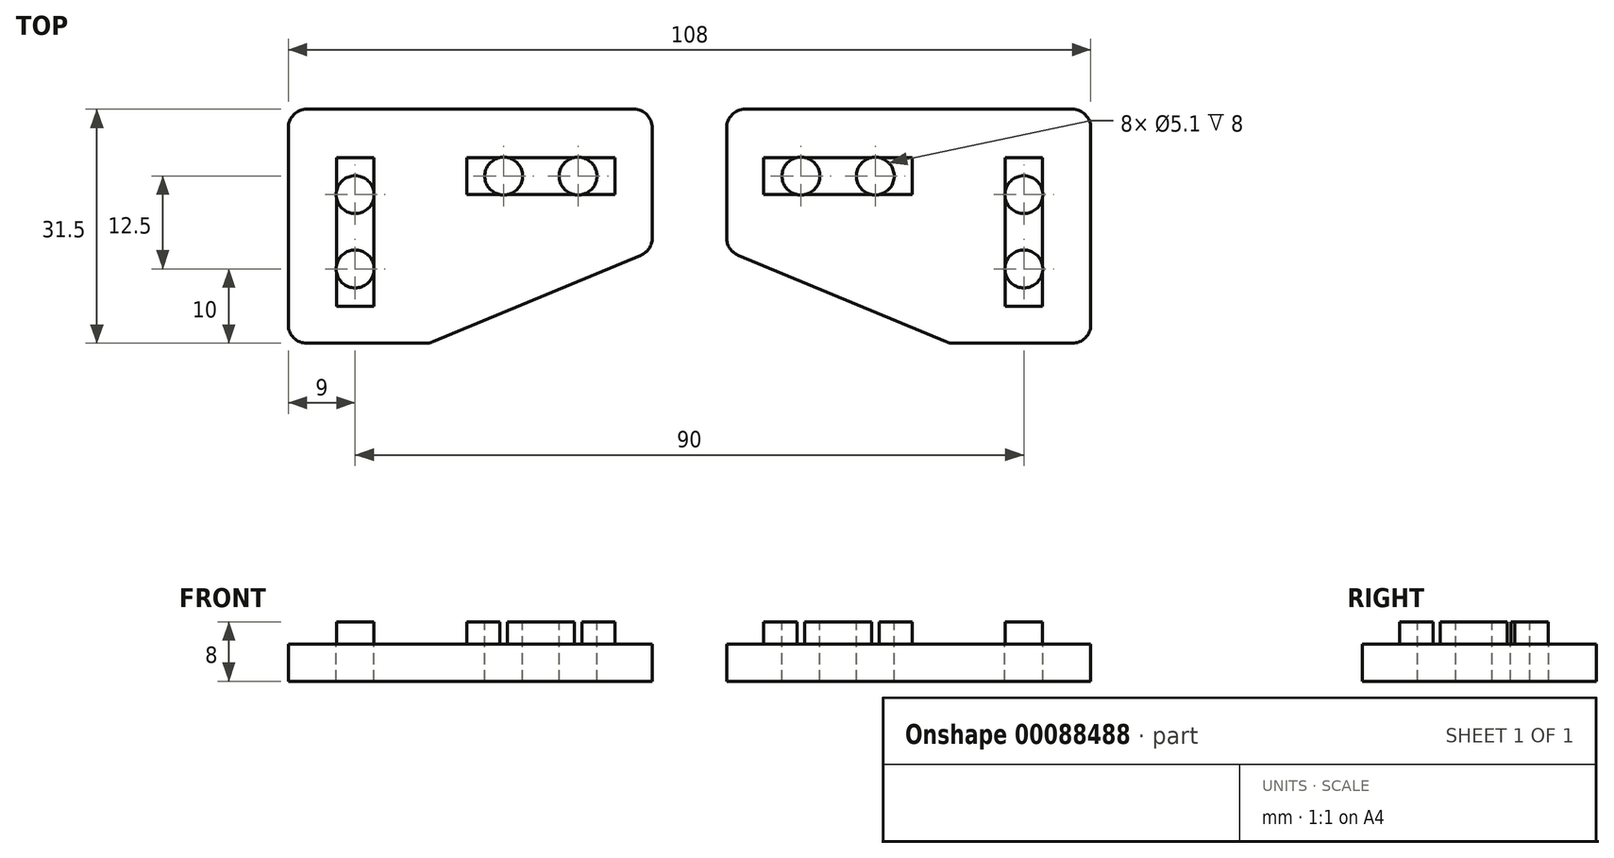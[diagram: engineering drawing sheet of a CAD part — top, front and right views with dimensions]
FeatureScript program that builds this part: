
annotation { "Feature Type Name" : "Feature", "Feature Type Description" : "" }
export const myFeature = defineFeature(function(context is Context, id is Id, definition is map)
    precondition{}
    {
        {
            var Q0;
            Q0=qCreatedBy(makeId("Top.planeOp"),FACE);
            var sketch = newSketch(context, id + "F0", { "sketchPlane" : qUnion([Q0])});
            skLineSegment(sketch, "E0", {"start": v(-9, -1) * mm, "end": v(40, -1) * mm});
            skLineSegment(sketch, "E1", {"start": v(40, -1) * mm, "end": v(40, -20) * mm});
            skLineSegment(sketch, "E2", {"start": v(-9, -1) * mm, "end": v(-9, -32.5) * mm});
            skLineSegment(sketch, "E3", {"start": v(-9, -32.5) * mm, "end": v(10, -32.5) * mm});
            skLineSegment(sketch, "E4.bottom", {"start": v(2.5, -7.5) * mm, "end": v(-2.5, -7.5) * mm, "construction": true});
            skLineSegment(sketch, "E4.top", {"start": v(2.5, -27.5) * mm, "end": v(-2.5, -27.5) * mm, "construction": true});
            skLineSegment(sketch, "E4.left", {"start": v(2.5, -7.5) * mm, "end": v(2.5, -27.5) * mm, "construction": true});
            skLineSegment(sketch, "E4.right", {"start": v(-2.5, -7.5) * mm, "end": v(-2.5, -27.5) * mm, "construction": true});
            skPoint(sketch, "E4.middle", {"position": v(0, -17.5) * mm});
            skLineSegment(sketch, "E5.bottom", {"start": v(15, -7.5) * mm, "end": v(35, -7.5) * mm, "construction": true});
            skLineSegment(sketch, "E5.top", {"start": v(15, -12.5) * mm, "end": v(35, -12.5) * mm, "construction": true});
            skLineSegment(sketch, "E5.left", {"start": v(15, -7.5) * mm, "end": v(15, -12.5) * mm, "construction": true});
            skLineSegment(sketch, "E5.right", {"start": v(35, -7.5) * mm, "end": v(35, -12.5) * mm, "construction": true});
            skPoint(sketch, "E5.middle", {"position": v(25, -10) * mm});
            skLineSegment(sketch, "E6", {"start": v(10, -32.5) * mm, "end": v(40, -20) * mm});
            skSolve(sketch);
        }
        {
            var Q0;
            Q0=makeQuery(id+"F0.imprint","IMPRINT",FACE,{"disambiguationData":[TD([[makeQuery(id+"F0.imprint","IMPRINT",EDGE,{"derivedFrom":sQuery(id+"F0.wireOp",EDGE,"E0")}),-1.0]])]});
            extrude(context, id + "F1", {"entities" : qUnion([Q0]), "oppositeDirection" : true, "depth" : 5 * mm});
        }
        {
            var Q0;
            Q0=qCreatedBy(makeId("Top.planeOp"),FACE);
            var sketch = newSketch(context, id + "F2", { "sketchPlane" : qUnion([Q0])});
            skLineSegment(sketch, "E7.0", {"start": v(2.5, -7.5) * mm, "end": v(-2.5, -7.5) * mm});
            skLineSegment(sketch, "E8.0", {"start": v(-2.5, -7.5) * mm, "end": v(-2.5, -27.5) * mm});
            skLineSegment(sketch, "E9.0", {"start": v(2.5, -7.5) * mm, "end": v(2.5, -27.5) * mm});
            skLineSegment(sketch, "E10.0", {"start": v(2.5, -27.5) * mm, "end": v(-2.5, -27.5) * mm});
            skLineSegment(sketch, "E11.0", {"start": v(15, -7.5) * mm, "end": v(15, -12.5) * mm});
            skLineSegment(sketch, "E12.0", {"start": v(15, -7.5) * mm, "end": v(35, -7.5) * mm});
            skLineSegment(sketch, "E13.0", {"start": v(15, -12.5) * mm, "end": v(35, -12.5) * mm});
            skLineSegment(sketch, "E14.0", {"start": v(35, -7.5) * mm, "end": v(35, -12.5) * mm});
            skSolve(sketch);
        }
        {
            var Q0;
            Q0 = qSketchRegion(id + "F2", true);
            extrude(context, id + "F3", {"entities" : qUnion([Q0]), "operationType" : NewBodyOperationType.ADD, "depth" : 3 * mm});
        }
        {
            var Q0;
            Q0=makeQuery(id+"F3.opExtrude","CAP_FACE",FACE,{"disambiguationData":[OSD([sQuery(id+"F2.wireOp",EDGE,"E7.0"),sQuery(id+"F2.wireOp",EDGE,"E8.0"),sQuery(id+"F2.wireOp",EDGE,"E9.0"),sQuery(id+"F2.wireOp",EDGE,"E10.0")])],"isStart":false});
            var sketch = newSketch(context, id + "F4", { "sketchPlane" : qUnion([Q0])});
            skCircle(sketch, "E15", {"center": v(0, -12.5) * mm, "radius": 2.55 * mm});
            skPoint(sketch, "E15.centerSnap0", {"position": v(0, -7.5) * mm});
            skCircle(sketch, "E16", {"center": v(0, -22.5) * mm, "radius": 2.55 * mm});
            skCircle(sketch, "E17", {"center": v(20, -10) * mm, "radius": 2.55 * mm});
            skCircle(sketch, "E18", {"center": v(30, -10) * mm, "radius": 2.55 * mm});
            skLineSegment(sketch, "E19", {"start": v(0, -12.5) * mm, "end": v(0, -22.5) * mm});
            skLineSegment(sketch, "E20", {"start": v(20, -10) * mm, "end": v(30, -10) * mm});
            skSolve(sketch);
        }
        {
            var Q0;
            Q0 = qSketchRegion(id + "F4", true);
            extrude(context, id + "F5", {"entities" : qUnion([Q0]), "operationType" : NewBodyOperationType.REMOVE, "oppositeDirection" : true, "depth" : 10 * mm});
        }
        {
            var Q0;
            Q0=makeQuery(id+"F1.opExtrude","SWEPT_EDGE",EDGE,{"disambiguationData":[OSD([sQuery(id+"F0.wireOp",EDGE,"E0"),sQuery(id+"F0.wireOp",EDGE,"E2")])]});
            var Q1;
            Q1=makeQuery(id+"F1.opExtrude","SWEPT_EDGE",EDGE,{"disambiguationData":[OSD([sQuery(id+"F0.wireOp",EDGE,"E2"),sQuery(id+"F0.wireOp",EDGE,"E3")])]});
            var Q2;
            Q2=makeQuery(id+"F1.opExtrude","SWEPT_EDGE",EDGE,{"disambiguationData":[OSD([sQuery(id+"F0.wireOp",EDGE,"E3"),sQuery(id+"F0.wireOp",EDGE,"E6")])]});
            var Q3;
            Q3=makeQuery(id+"F1.opExtrude","SWEPT_EDGE",EDGE,{"disambiguationData":[OSD([sQuery(id+"F0.wireOp",EDGE,"E1"),sQuery(id+"F0.wireOp",EDGE,"E6")])]});
            var Q4;
            Q4=makeQuery(id+"F1.opExtrude","SWEPT_EDGE",EDGE,{"disambiguationData":[OSD([sQuery(id+"F0.wireOp",EDGE,"E0"),sQuery(id+"F0.wireOp",EDGE,"E1")])]});
            fillet(context, id + "F6", {"entities" : qUnion([Q0, Q1, Q2, Q3, Q4]), "radius" : 2.5 * mm, "tangentPropagation" : true, "allowEdgeOverflow" : false});
        }
        {
            var Q0;
            Q0=makeQuery(id+"F1.opExtrude","SWEPT_FACE",FACE,{"disambiguationData":[OSD([sQuery(id+"F0.wireOp",EDGE,"E1")])]});
            cPlane(context, id + "F7", {"entities" : qUnion([Q0]), "cplaneType" : CPlaneType.OFFSET, "offset" : 5 * mm, "width" : 150 * mm, "height" : 150 * mm});
        }
        {
            var Q0;
            Q0=makeQuery(id+"F1.opExtrude","SWEPT_BODY",BODY,{"disambiguationData":[OSD([sQuery(id+"F0.wireOp",EDGE,"E0"),sQuery(id+"F0.wireOp",EDGE,"E1"),sQuery(id+"F0.wireOp",EDGE,"E2"),sQuery(id+"F0.wireOp",EDGE,"E3"),sQuery(id+"F0.wireOp",EDGE,"E6")])]});
            var Q1;
            Q1=qCreatedBy(id+"F7.planeOp",FACE);
            mirror(context, id + "F8", {"entities" : qUnion([Q0]), "mirrorPlane" : qUnion([Q1])});
        }
    });
